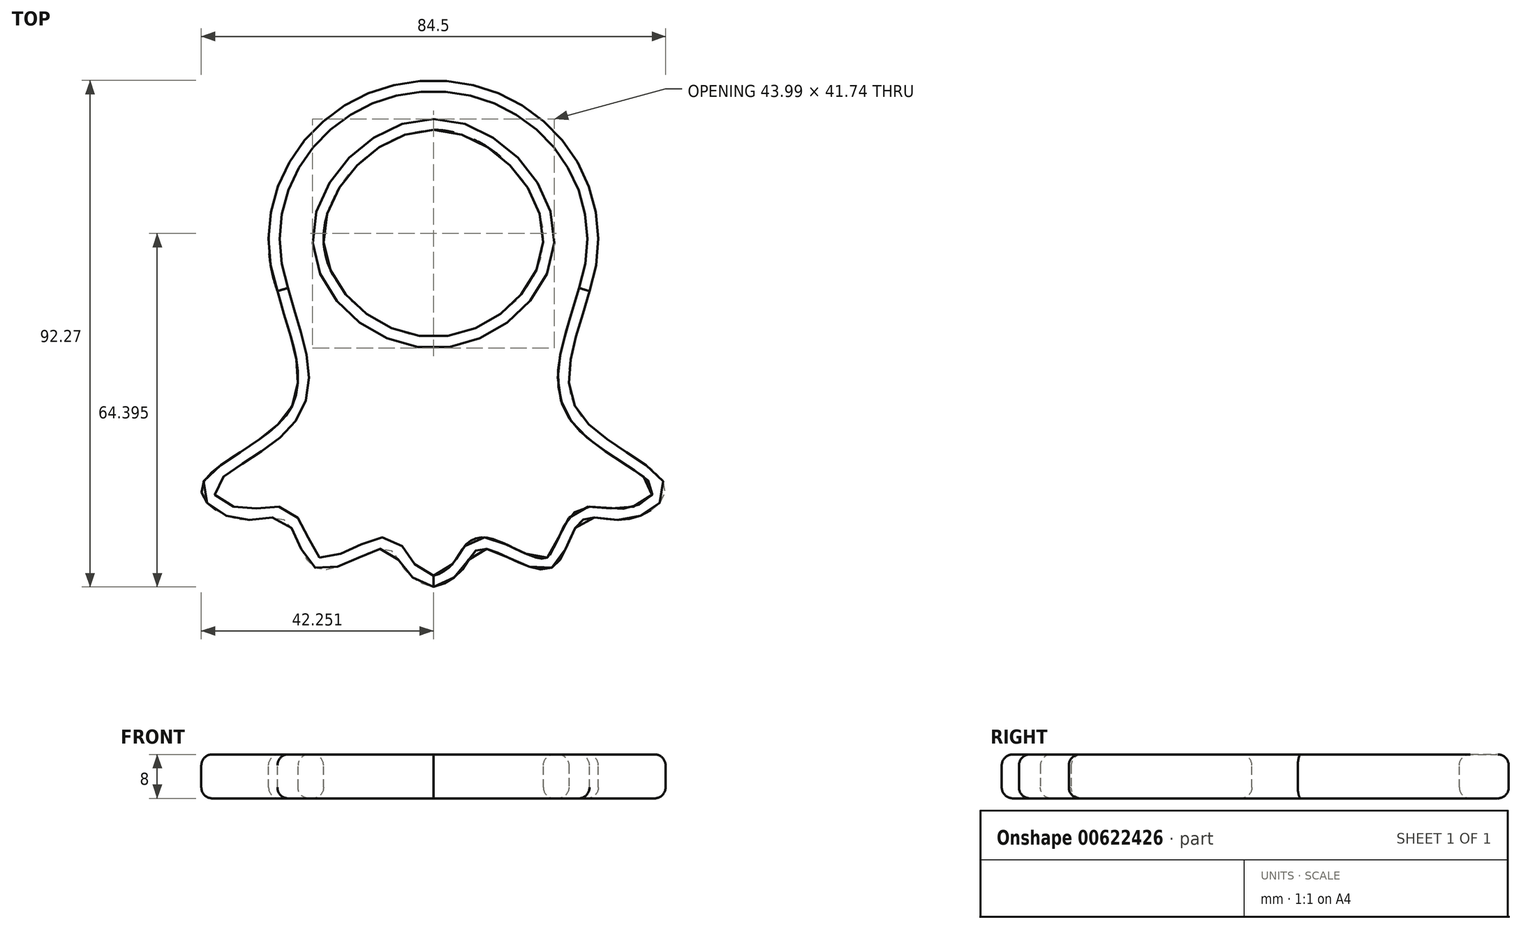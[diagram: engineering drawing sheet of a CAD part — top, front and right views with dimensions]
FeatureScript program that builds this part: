
annotation { "Feature Type Name" : "Feature", "Feature Type Description" : "" }
export const myFeature = defineFeature(function(context is Context, id is Id, definition is map)
    precondition{}
    {
        {
            var Q0;
            Q0=qCreatedBy(makeId("Top.planeOp"),FACE);
            var sketch = newSketch(context, id + "F0", { "sketchPlane" : qUnion([Q0])});
            skEllipse(sketch, "E0", {"center": v(0, 22.43) * mm, "majorRadius": 30 * mm, "minorRadius": 29 * mm, "majorAxis": v(1, 0)});
            skPoint(sketch, "E1.1.internal.snap0", {"position": v(-18.1, 22.43) * mm});
            skPoint(sketch, "E1.3.internal.snap0", {"position": v(17.61, 22.43) * mm});
            skFitSpline(sketch, "E1", {"points": [v(0, 42.43) * mm, v(-20, 22.43) * mm, v(0, 4.68) * mm, v(20, 22.43) * mm, v(0, 42.43) * mm]});
            skPoint(sketch, "E2", {"position": v(-30, 22.43) * mm});
            skPoint(sketch, "E3", {"position": v(30, 22.43) * mm});
            skPoint(sketch, "E4", {"position": v(0, 51.43) * mm});
            skPoint(sketch, "E5", {"position": v(0, -6.57) * mm});
            skFitSpline(sketch, "E6", {"points": [v(-28.39, 13.05) * mm, v(-26.2, -8.72) * mm, v(-42.19, -22.55) * mm, v(-35.15, -28.55) * mm, v(-26.74, -28.91) * mm, v(-21.01, -37.56) * mm, v(-8.57, -33.82) * mm, v(0, -40.84) * mm], "startDerivative": vector(29.98, -119.45) * mm, "endDerivative": vector(149.53, -34.13) * mm});
            skFitSpline(sketch, "E7.MirrorCS", {"points": [v(28.39, 13.05) * mm, v(26.2, -8.72) * mm, v(42.19, -22.55) * mm, v(35.15, -28.55) * mm, v(26.74, -28.91) * mm, v(21.01, -37.56) * mm, v(8.57, -33.82) * mm, v(0, -40.84) * mm], "startDerivative": vector(-29.98, -119.45) * mm, "endDerivative": vector(-149.53, -34.13) * mm});
            skSolve(sketch);
        }
        {
            var Q0;
            {var subQ0=sQuery(id+"F0.wireOp",EDGE,"E6");Q0=makeQuery(id+"F0.imprint","IMPRINT",FACE,{"disambiguationData":[TD([[makeQuery(id+"F0.imprint","IMPRINT",EDGE,{"derivedFrom":subQ0}),1.0]])]});}
            var Q1;
            Q1=makeQuery(id+"F0.imprint","IMPRINT",FACE,{"disambiguationData":[TD([[makeQuery(id+"F0.imprint","IMPRINT",EDGE,{"derivedFrom":sQuery(id+"F0.wireOp",EDGE,"E1")}),-1.0]])]});
            extrude(context, id + "F1", {"entities" : qUnion([Q0, Q1]), "oppositeDirection" : true, "depth" : 8 * mm, "offsetDistance" : 25 * mm});
        }
        {
            var Q0;
            Q0=makeQuery(id+"F1.opExtrude","CAP_EDGE",EDGE,{"disambiguationData":[OSD([sQuery(id+"F0.wireOp",EDGE,"E1")])],"isStart":true});
            var Q1;
            Q1=makeQuery(id+"F1.opExtrude","CAP_EDGE",EDGE,{"disambiguationData":[OSD([sQuery(id+"F0.wireOp",EDGE,"E6")])],"isStart":true});
            var Q2;
            Q2=makeQuery(id+"F1.opExtrude","CAP_EDGE",EDGE,{"disambiguationData":[OSD([sQuery(id+"F0.wireOp",EDGE,"E7.MirrorCS")])],"isStart":true});
            var Q3;
            Q3=makeQuery(id+"F1.opExtrude","CAP_EDGE",EDGE,{"disambiguationData":[OSD([sQuery(id+"F0.wireOp",EDGE,"E0")])],"isStart":true});
            var Q4;
            Q4=makeQuery(id+"F1.opExtrude","CAP_FACE",FACE,{"disambiguationData":[OSD([sQuery(id+"F0.wireOp",EDGE,"E0"),sQuery(id+"F0.wireOp",EDGE,"E1"),sQuery(id+"F0.wireOp",EDGE,"E6"),sQuery(id+"F0.wireOp",EDGE,"E7.MirrorCS")])],"isStart":false});
            fillet(context, id + "F2", {"entities" : qUnion([Q0, Q1, Q2, Q3, Q4]), "radius" : 2 * mm, "tangentPropagation" : true, "allowEdgeOverflow" : false});
        }
    });
